# Revit family: Proxway_Лифтовой_IP-контроллер_PW-E_v.2
name_source: partatom
category: Электрооборудование
units: mm (PartAtom-declared; Revit-internal decimal feet)

## family parameters
Всегда вертикально = Нет
На основе рабочей плоскости = Нет
Общий = Да
При загрузке вырезать с полостями = Нет
Размер круглого соединителя = Использовать диаметр
Тип детали = Другая панель
Точка расчета площади = Да

## types (2) — shared parameters
=Габариты= = =Габариты=
ADSK_Единица измерения = шт.
ADSK_Завод-изготовитель = Proxway
ADSK_Код изделия = PW-E v.2
ADSK_Количество = 1
ADSK_Марка = PW-E v.2
ADSK_Наименование = Лифтовой IP контроллер PW-E v.2
ADSK_Обозначение = КД
ADSK_Раздел спецификации = 2. Центральное оборудование
ADSK_Размер_Высота = 300 мм
ADSK_Размер_Глубина = 100 мм
ADSK_Размер_Ширина = 220 мм
ADSK_Ток дежурного режима = 250.000 мА
ADSK_Ток тревожного режима = 250.000 мА
URL = https://proxway-ble.ru
АКБ_Наименование = Батарея аккумуляторная свинцово-кислотная 12В 7Ач
АКБ_Тип = 1207
Зона обслуживания_Отступ от прибора = 50 мм
УГО_Тип = УГО_СС_Контроллер
zero-valued in all types: Отметка по умолчанию

## per-type parameters (varying)
| type | ADSK_Тип | Наличие АКБ | Текст модели |
| PW-E v.2 без АКБ |  | Нет | PW-E v.2 |
| PW-E v.2 с АКБ | с АКБ | Да | PW-E v.2 АКБ |
